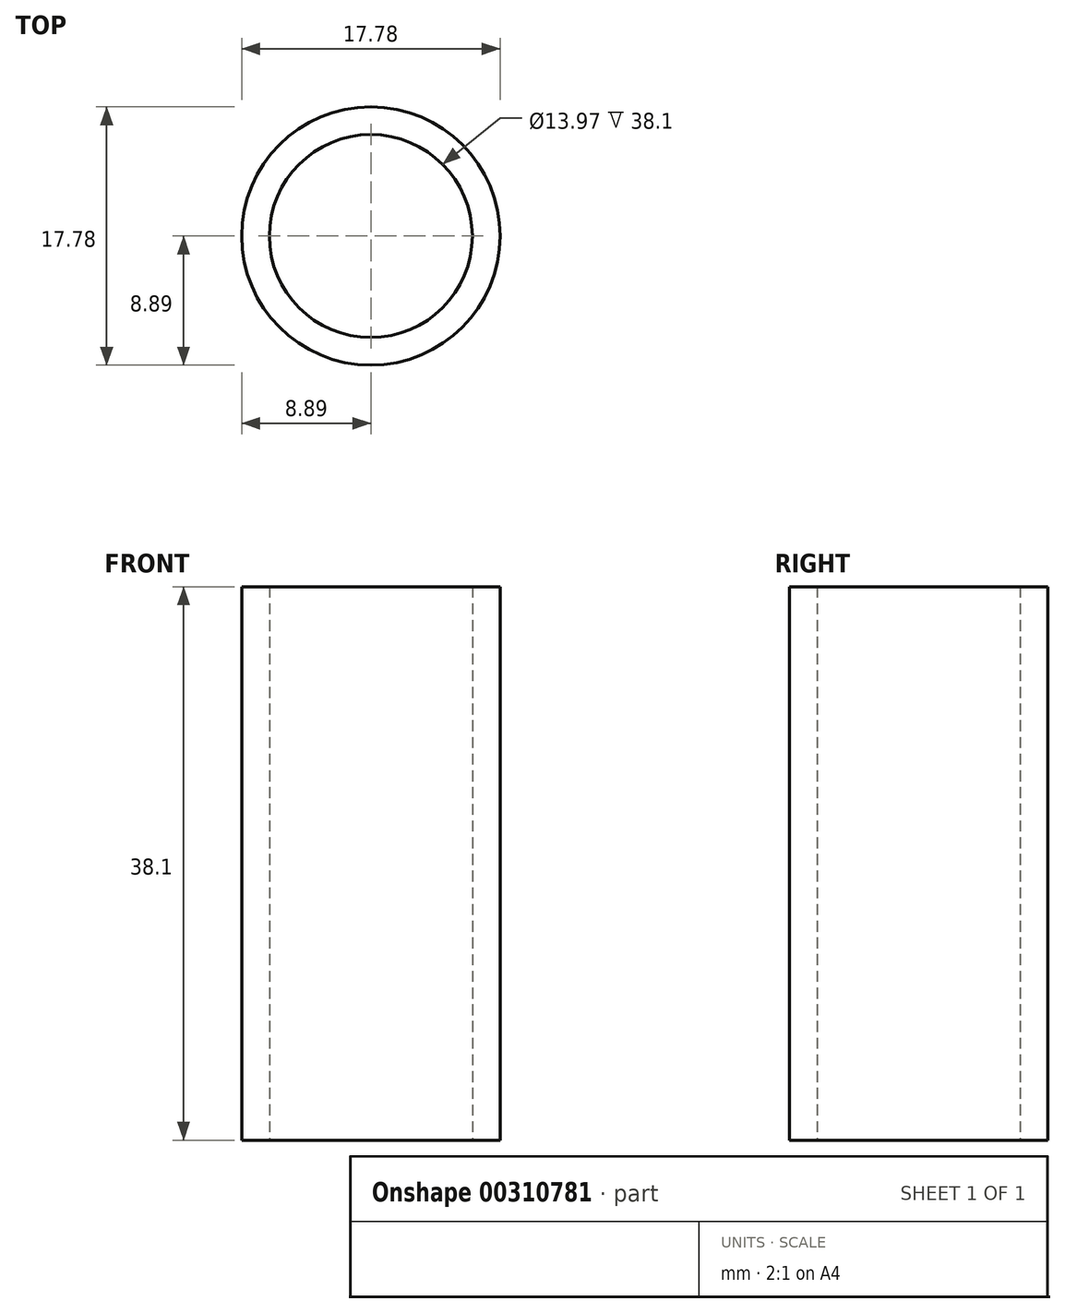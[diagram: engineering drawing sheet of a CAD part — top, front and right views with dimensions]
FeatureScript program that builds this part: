
annotation { "Feature Type Name" : "Feature", "Feature Type Description" : "" }
export const myFeature = defineFeature(function(context is Context, id is Id, definition is map)
    precondition{}
    {
        {
            var Q0;
            Q0=qCreatedBy(makeId("Top.planeOp"),FACE);
            var sketch = newSketch(context, id + "F0", { "sketchPlane" : qUnion([Q0])});
            skCircle(sketch, "E0", {"center": v(0, 0) * mm, "radius": 8.9 * mm});
            skCircle(sketch, "E1", {"center": v(0, 0) * mm, "radius": 6.99 * mm});
            skSolve(sketch);
        }
        {
            var Q0;
            Q0=makeQuery(id+"F0.imprint","IMPRINT",FACE,{"disambiguationData":[TD([[makeQuery(id+"F0.imprint","IMPRINT",EDGE,{"derivedFrom":sQuery(id+"F0.wireOp",EDGE,"E0")}),1.0]])]});
            extrude(context, id + "F1", {"entities" : qUnion([Q0]), "depth" : 38.1 * mm});
        }
    });
